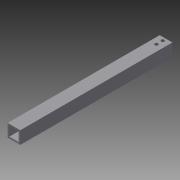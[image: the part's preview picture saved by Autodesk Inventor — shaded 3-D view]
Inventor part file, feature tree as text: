
AUTODESK INVENTOR PART (.ipt)
format: ipt  version: 2013 (Build 170138000, 138)  size: 96,768 bytes
history: native  units: in
note: dims shown in document units (in); Inventor stores cm internally (conversion verified against a paired STEP export)
features: extrude x2, sketch x2, reference x2
ambient origin geometry x8: Origin, YZ Plane, XZ Plane, XY Plane, X Axis, Y Axis, Z Axis, Center Point
bodies: Solid1 (feature_tree)
feature tree (6):
  extrude  "Extrusion1"  Depth=1.0in
  extrude  "Extrusion2"  Depth=12.0in TaperAngle=0.0deg
  sketch  "Sketch1"  dims[d0=1.0in d2=1.0in]
  sketch  "Sketch2"  dims[d3=0.125in d4=12.0in d5=0.0in d6=1.0in d7=0.0in]
  reference  "Reference1"
  reference  "Reference2"
